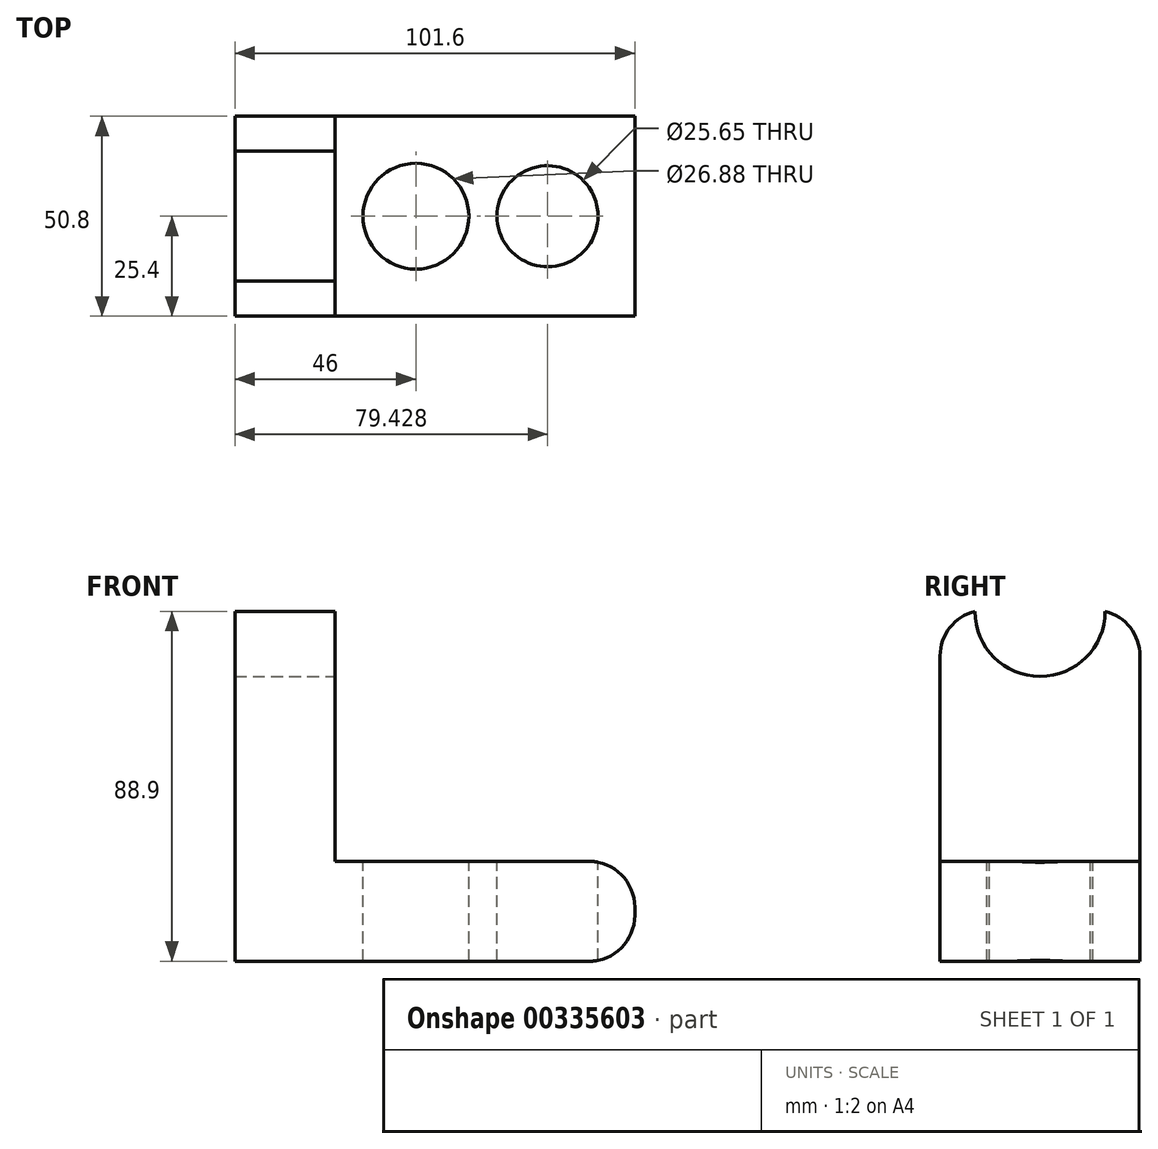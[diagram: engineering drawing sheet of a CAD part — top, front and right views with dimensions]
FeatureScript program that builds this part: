
annotation { "Feature Type Name" : "Feature", "Feature Type Description" : "" }
export const myFeature = defineFeature(function(context is Context, id is Id, definition is map)
    precondition{}
    {
        {
            var Q0;
            Q0=qCreatedBy(makeId("Front.planeOp"),FACE);
            var sketch = newSketch(context, id + "F0", { "sketchPlane" : qUnion([Q0])});
            skLineSegment(sketch, "E0", {"start": v(-46, -39.15) * mm, "end": v(55.6, -39.15) * mm});
            skLineSegment(sketch, "E1", {"start": v(55.6, -39.15) * mm, "end": v(55.6, -13.75) * mm});
            skLineSegment(sketch, "E2", {"start": v(55.6, -13.75) * mm, "end": v(-20.6, -13.75) * mm});
            skLineSegment(sketch, "E3", {"start": v(-46, -39.15) * mm, "end": v(-46, 49.75) * mm});
            skLineSegment(sketch, "E4", {"start": v(-46, 49.75) * mm, "end": v(-20.6, 49.75) * mm});
            skLineSegment(sketch, "E5", {"start": v(-20.6, 49.75) * mm, "end": v(-20.6, -13.75) * mm});
            skSolve(sketch);
        }
        {
            var Q0;
            Q0 = qSketchRegion(id + "F0", true);
            extrude(context, id + "F1", {"entities" : qUnion([Q0]), "depth" : 50.8 * mm});
        }
        {
            var Q0;
            Q0=makeQuery(id+"F1.opExtrude","SWEPT_FACE",FACE,{"disambiguationData":[OSD([sQuery(id+"F0.wireOp",EDGE,"E5")])]});
            var sketch = newSketch(context, id + "F2", { "sketchPlane" : qUnion([Q0])});
            skLineSegment(sketch, "E6", {"start": v(-25.4, -13.75) * mm, "end": v(-25.4, 11.65) * mm});
            skLineSegment(sketch, "E7", {"start": v(-50.8, 49.75) * mm, "end": v(-38.1, 49.75) * mm});
            skLineSegment(sketch, "E8", {"start": v(0, 49.75) * mm, "end": v(-12.7, 49.75) * mm});
            skArc(sketch, "E9", {"start": v(-41.93, 49.75) * mm, "mid": v(-25.4, 33.22) * mm, "end": v(-8.87, 49.75) * mm});
            skLineSegment(sketch, "E10", {"start": v(-50.8, 49.75) * mm, "end": v(0, 49.75) * mm});
            skSolve(sketch);
        }
        {
            var Q0;
            {var subQ0=sQuery(id+"F2.wireOp",EDGE,"E9");Q0=makeQuery(id+"F2.imprint","IMPRINT",FACE,{"disambiguationData":[TD([[makeQuery(id+"F2.imprint","IMPRINT",EDGE,{"derivedFrom":subQ0}),1.0]])]});}
            extrude(context, id + "F3", {"entities" : qUnion([Q0]), "operationType" : NewBodyOperationType.REMOVE, "oppositeDirection" : true, "depth" : 25.4 * mm});
        }
        {
            var Q0;
            Q0=makeQuery(id+"F1.opExtrude","SWEPT_FACE",FACE,{"disambiguationData":[OSD([sQuery(id+"F0.wireOp",EDGE,"E2")])]});
            var sketch = newSketch(context, id + "F4", { "sketchPlane" : qUnion([Q0])});
            skCircle(sketch, "E11", {"center": v(0, -25.4) * mm, "radius": 13.44 * mm});
            skPoint(sketch, "E11.centerSnap0", {"position": v(-20.6, -25.4) * mm});
            skCircle(sketch, "E12", {"center": v(33.43, -25.4) * mm, "radius": 12.83 * mm});
            skSolve(sketch);
        }
        {
            var Q0;
            Q0 = qSketchRegion(id + "F4", true);
            extrude(context, id + "F5", {"entities" : qUnion([Q0]), "operationType" : NewBodyOperationType.REMOVE, "oppositeDirection" : true, "depth" : 50.8 * mm});
        }
        {
            var Q0;
            Q0=makeQuery(id+"F1.opExtrude","CAP_EDGE",EDGE,{"disambiguationData":[OSD([sQuery(id+"F0.wireOp",EDGE,"E4")])],"isStart":false});
            var Q1;
            Q1=makeQuery(id+"F1.opExtrude","CAP_EDGE",EDGE,{"disambiguationData":[OSD([sQuery(id+"F0.wireOp",EDGE,"E4")])],"isStart":true});
            var Q2;
            Q2=makeQuery(id+"F1.opExtrude","SWEPT_EDGE",EDGE,{"disambiguationData":[OSD([sQuery(id+"F0.wireOp",EDGE,"E1"),sQuery(id+"F0.wireOp",EDGE,"E2")])]});
            var Q3;
            Q3=makeQuery(id+"F1.opExtrude","SWEPT_EDGE",EDGE,{"disambiguationData":[OSD([sQuery(id+"F0.wireOp",EDGE,"E0"),sQuery(id+"F0.wireOp",EDGE,"E1")])]});
            fillet(context, id + "F6", {"entities" : qUnion([Q0, Q1, Q2, Q3]), "radius" : 11.65 * mm, "tangentPropagation" : true, "allowEdgeOverflow" : false});
        }
    });
